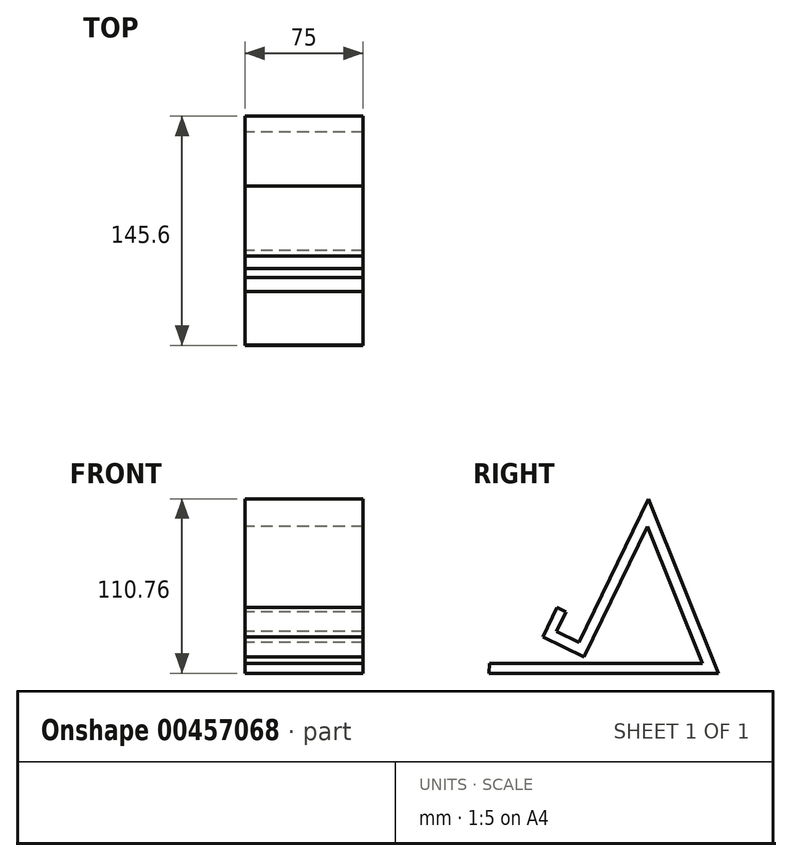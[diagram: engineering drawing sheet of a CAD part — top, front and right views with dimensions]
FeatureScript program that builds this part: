
annotation { "Feature Type Name" : "Feature", "Feature Type Description" : "" }
export const myFeature = defineFeature(function(context is Context, id is Id, definition is map)
    precondition{}
    {
        {
            var Q0;
            Q0=qCreatedBy(makeId("Right.planeOp"),FACE);
            var sketch = newSketch(context, id + "F0", { "sketchPlane" : qUnion([Q0])});
            skLineSegment(sketch, "E0", {"start": v(-73.08, -45.04) * mm, "end": v(72.52, -45.04) * mm});
            skLineSegment(sketch, "E1", {"start": v(72.52, -45.04) * mm, "end": v(28.04, 65.72) * mm});
            skLineSegment(sketch, "E2", {"start": v(28.04, 65.72) * mm, "end": v(-16.15, -25.5) * mm});
            skLineSegment(sketch, "E3", {"start": v(-16.15, -25.5) * mm, "end": v(-30.41, -18.58) * mm});
            skLineSegment(sketch, "E4", {"start": v(-30.41, -18.58) * mm, "end": v(-24.3, -6) * mm});
            skLineSegment(sketch, "E5", {"start": v(-24.3, -6) * mm, "end": v(-29.96, -3.26) * mm});
            skLineSegment(sketch, "E6", {"start": v(-29.96, -3.26) * mm, "end": v(-38.97, -21.85) * mm});
            skLineSegment(sketch, "E7", {"start": v(-38.97, -21.85) * mm, "end": v(-12.75, -34.56) * mm});
            skLineSegment(sketch, "E8", {"start": v(-12.75, -34.56) * mm, "end": v(27.41, 48.33) * mm});
            skLineSegment(sketch, "E9", {"start": v(27.41, 48.33) * mm, "end": v(62.43, -38.88) * mm});
            skLineSegment(sketch, "E10", {"start": v(62.43, -38.88) * mm, "end": v(-72.8, -38.88) * mm});
            skLineSegment(sketch, "E11", {"start": v(-72.8, -38.88) * mm, "end": v(-73.08, -45.04) * mm});
            skSolve(sketch);
        }
        {
            var Q0;
            Q0=makeQuery(id+"F0.imprint","IMPRINT",FACE,{"disambiguationData":[TD([[makeQuery(id+"F0.imprint","IMPRINT",EDGE,{"derivedFrom":sQuery(id+"F0.wireOp",EDGE,"E0")}),1.0]])]});
            extrude(context, id + "F1", {"entities" : qUnion([Q0]), "depth" : 75 * mm});
        }
    });
